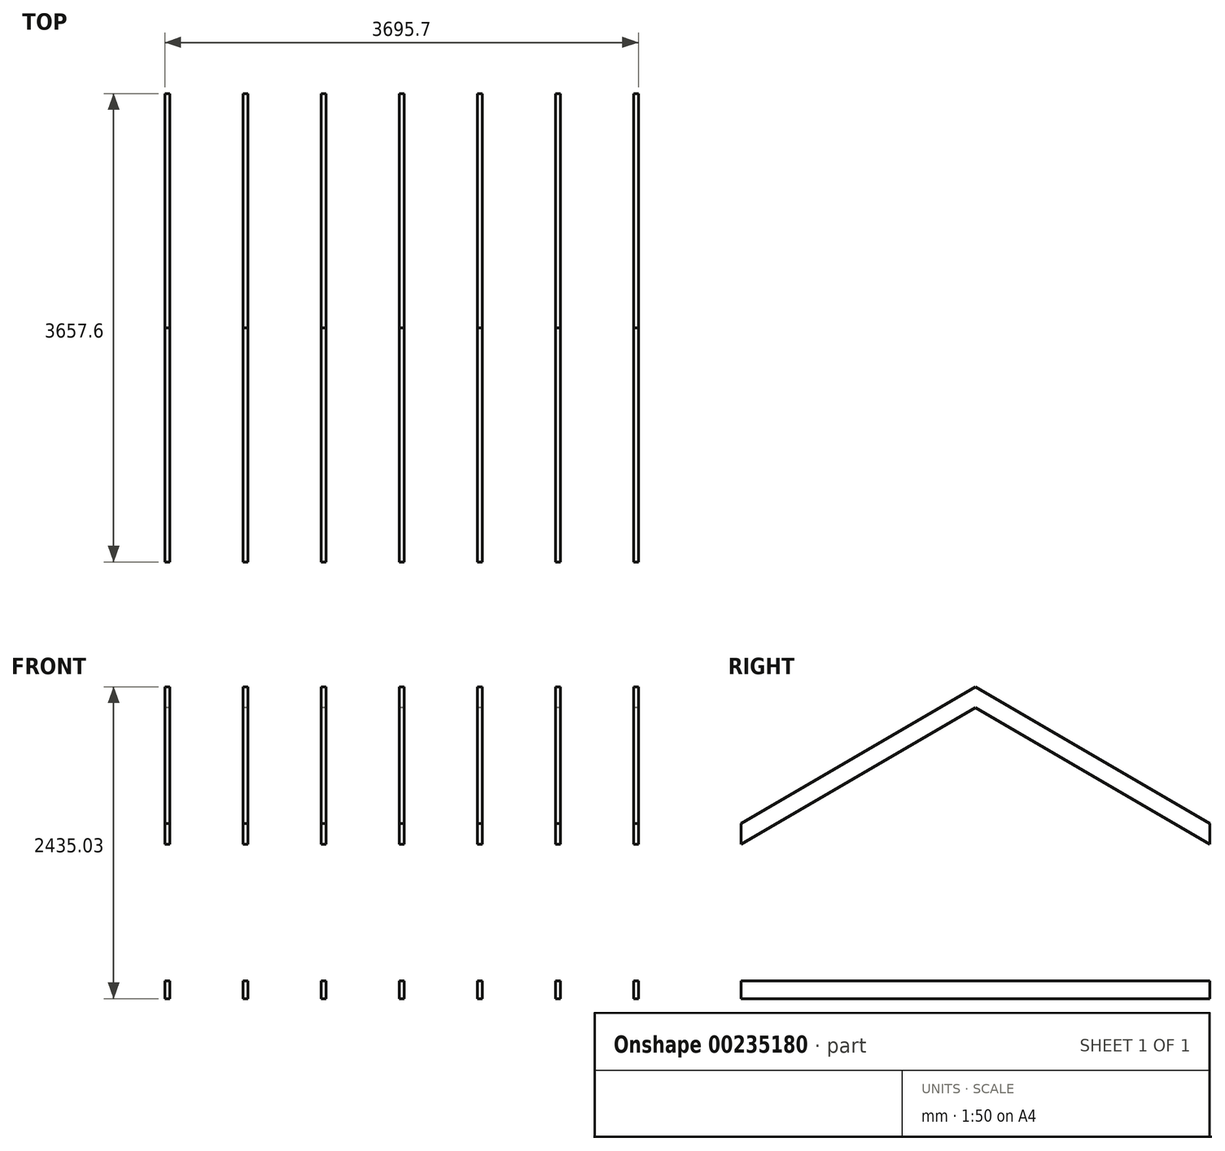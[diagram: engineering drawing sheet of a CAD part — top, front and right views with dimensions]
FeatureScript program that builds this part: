
annotation { "Feature Type Name" : "Feature", "Feature Type Description" : "" }
export const myFeature = defineFeature(function(context is Context, id is Id, definition is map)
    precondition{}
    {
        {
            var Q0;
            Q0=qCreatedBy(makeId("Right.planeOp"),FACE);
            var sketch = newSketch(context, id + "F0", { "sketchPlane" : qUnion([Q0])});
            skLineSegment(sketch, "E0", {"start": v(0, 0) * mm, "end": v(3657.6, 0) * mm});
            skLineSegment(sketch, "E1", {"start": v(3657.6, 0) * mm, "end": v(3657.6, -139.7) * mm});
            skLineSegment(sketch, "E2", {"start": v(3657.6, -139.7) * mm, "end": v(0, -139.7) * mm});
            skLineSegment(sketch, "E3", {"start": v(0, -139.7) * mm, "end": v(0, 0) * mm});
            skLineSegment(sketch, "E4", {"start": v(0, 1066.8) * mm, "end": v(1828.8, 2133.6) * mm});
            skPoint(sketch, "E4.endSnap0", {"position": v(1828.8, 0) * mm});
            skLineSegment(sketch, "E5", {"start": v(1828.8, 2133.6) * mm, "end": v(3657.6, 1066.8) * mm});
            skLineSegment(sketch, "E6", {"start": v(3657.6, 1066.8) * mm, "end": v(3657.6, 1228.53) * mm});
            skLineSegment(sketch, "E7", {"start": v(3657.6, 1228.53) * mm, "end": v(1828.8, 2295.33) * mm});
            skLineSegment(sketch, "E8", {"start": v(1828.8, 2295.33) * mm, "end": v(0, 1228.53) * mm});
            skLineSegment(sketch, "E9", {"start": v(0, 1228.53) * mm, "end": v(0, 1066.8) * mm});
            skSolve(sketch);
        }
        {
            var Q0;
            Q0=makeQuery(id+"F0.imprint","IMPRINT",FACE,{"disambiguationData":[TD([[makeQuery(id+"F0.imprint","IMPRINT",EDGE,{"derivedFrom":sQuery(id+"F0.wireOp",EDGE,"E0")}),-1.0]])]});
            var Q1;
            Q1=makeQuery(id+"F0.imprint","IMPRINT",FACE,{"disambiguationData":[TD([[makeQuery(id+"F0.imprint","IMPRINT",EDGE,{"derivedFrom":sQuery(id+"F0.wireOp",EDGE,"E4")}),1.0]])]});
            extrude(context, id + "F1", {"entities" : qUnion([Q0, Q1]), "depth" : 3962.4 * mm});
        }
        {
            var Q0;
            Q0=makeQuery(id+"F1.opExtrude","SWEPT_FACE",FACE,{"disambiguationData":[OSD([sQuery(id+"F0.wireOp",EDGE,"E9")])]});
            var sketch = newSketch(context, id + "F2", { "sketchPlane" : qUnion([Q0])});
            skLineSegment(sketch, "E10.bottom", {"start": v(3924.3, -139.7) * mm, "end": v(3352.8, -139.7) * mm});
            skLineSegment(sketch, "E10.top", {"start": v(3924.3, 2295.33) * mm, "end": v(3352.8, 2295.33) * mm});
            skLineSegment(sketch, "E10.left", {"start": v(3924.3, -139.7) * mm, "end": v(3924.3, 2295.33) * mm});
            skLineSegment(sketch, "E10.right", {"start": v(3352.8, -139.7) * mm, "end": v(3352.8, 2295.33) * mm});
            skLineSegment(sketch, "E11.1.0.0", {"start": v(3314.7, 2295.33) * mm, "end": v(2743.2, 2295.33) * mm});
            skLineSegment(sketch, "E11.1.0.1", {"start": v(2743.2, -139.7) * mm, "end": v(2743.2, 2295.33) * mm});
            skLineSegment(sketch, "E11.1.0.2", {"start": v(3314.7, -139.7) * mm, "end": v(3314.7, 2295.33) * mm});
            skLineSegment(sketch, "E11.1.0.3", {"start": v(3314.7, -139.7) * mm, "end": v(2743.2, -139.7) * mm});
            skLineSegment(sketch, "E11.2.0.0", {"start": v(2705.1, 2295.33) * mm, "end": v(2133.6, 2295.33) * mm});
            skLineSegment(sketch, "E11.2.0.1", {"start": v(2133.6, -139.7) * mm, "end": v(2133.6, 2295.33) * mm});
            skLineSegment(sketch, "E11.2.0.2", {"start": v(2705.1, -139.7) * mm, "end": v(2705.1, 2295.33) * mm});
            skLineSegment(sketch, "E11.2.0.3", {"start": v(2705.1, -139.7) * mm, "end": v(2133.6, -139.7) * mm});
            skLineSegment(sketch, "E11.3.0.0", {"start": v(2095.5, 2295.33) * mm, "end": v(1524, 2295.33) * mm});
            skLineSegment(sketch, "E11.3.0.1", {"start": v(1524, -139.7) * mm, "end": v(1524, 2295.33) * mm});
            skLineSegment(sketch, "E11.3.0.2", {"start": v(2095.5, -139.7) * mm, "end": v(2095.5, 2295.33) * mm});
            skLineSegment(sketch, "E11.3.0.3", {"start": v(2095.5, -139.7) * mm, "end": v(1524, -139.7) * mm});
            skLineSegment(sketch, "E11.4.0.0", {"start": v(1485.9, 2295.33) * mm, "end": v(914.4, 2295.33) * mm});
            skLineSegment(sketch, "E11.4.0.1", {"start": v(914.4, -139.7) * mm, "end": v(914.4, 2295.33) * mm});
            skLineSegment(sketch, "E11.4.0.2", {"start": v(1485.9, -139.7) * mm, "end": v(1485.9, 2295.33) * mm});
            skLineSegment(sketch, "E11.4.0.3", {"start": v(1485.9, -139.7) * mm, "end": v(914.4, -139.7) * mm});
            skLineSegment(sketch, "E11.5.0.0", {"start": v(876.3, 2295.33) * mm, "end": v(304.8, 2295.33) * mm});
            skLineSegment(sketch, "E11.5.0.1", {"start": v(304.8, -139.7) * mm, "end": v(304.8, 2295.33) * mm});
            skLineSegment(sketch, "E11.5.0.2", {"start": v(876.3, -139.7) * mm, "end": v(876.3, 2295.33) * mm});
            skLineSegment(sketch, "E11.5.0.3", {"start": v(876.3, -139.7) * mm, "end": v(304.8, -139.7) * mm});
            skLineSegment(sketch, "E11.direction1", {"start": v(3352.8, 2295.33) * mm, "end": v(2743.2, 2295.33) * mm, "construction": true});
            skLineSegment(sketch, "E12.bottom", {"start": v(266.7, 2295.33) * mm, "end": v(0, 2295.33) * mm});
            skLineSegment(sketch, "E12.top", {"start": v(266.7, -139.7) * mm, "end": v(0, -139.7) * mm});
            skLineSegment(sketch, "E12.left", {"start": v(266.7, 2295.33) * mm, "end": v(266.7, -139.7) * mm});
            skLineSegment(sketch, "E12.right", {"start": v(0, 2295.33) * mm, "end": v(0, -139.7) * mm});
            skSolve(sketch);
        }
        {
            var Q0;
            {var subQ0=sQuery(id+"F2.wireOp",EDGE,"E12.top");Q0=makeQuery(id+"F2.imprint","IMPRINT",FACE,{"disambiguationData":[TD([[makeQuery(id+"F2.imprint","IMPRINT",EDGE,{"derivedFrom":subQ0}),-1.0]])]});}
            var Q1;
            {var subQ0=sQuery(id+"F2.wireOp",EDGE,"E11.4.0.3");Q1=makeQuery(id+"F2.imprint","IMPRINT",FACE,{"disambiguationData":[TD([[makeQuery(id+"F2.imprint","IMPRINT",EDGE,{"derivedFrom":subQ0}),-1.0]])]});}
            var Q2;
            {var subQ0=sQuery(id+"F2.wireOp",EDGE,"E11.3.0.3");Q2=makeQuery(id+"F2.imprint","IMPRINT",FACE,{"disambiguationData":[TD([[makeQuery(id+"F2.imprint","IMPRINT",EDGE,{"derivedFrom":subQ0}),-1.0]])]});}
            var Q3;
            {var subQ0=sQuery(id+"F2.wireOp",EDGE,"E11.2.0.3");Q3=makeQuery(id+"F2.imprint","IMPRINT",FACE,{"disambiguationData":[TD([[makeQuery(id+"F2.imprint","IMPRINT",EDGE,{"derivedFrom":subQ0}),-1.0]])]});}
            var Q4;
            {var subQ0=sQuery(id+"F2.wireOp",EDGE,"E11.1.0.3");Q4=makeQuery(id+"F2.imprint","IMPRINT",FACE,{"disambiguationData":[TD([[makeQuery(id+"F2.imprint","IMPRINT",EDGE,{"derivedFrom":subQ0}),-1.0]])]});}
            var Q5;
            {var subQ0=sQuery(id+"F2.wireOp",EDGE,"E10.bottom");Q5=makeQuery(id+"F2.imprint","IMPRINT",FACE,{"disambiguationData":[TD([[makeQuery(id+"F2.imprint","IMPRINT",EDGE,{"derivedFrom":subQ0}),-1.0]])]});}
            var Q6;
            {var subQ0=sQuery(id+"F2.wireOp",EDGE,"E10.left");var subQ1=sQuery(id+"F0.wireOp",EDGE,"E9");var subQ2=makeQuery(id+"F1.opExtrude","SWEPT_EDGE",EDGE,{"disambiguationData":[OSD([sQuery(id+"F0.wireOp",EDGE,"E4"),subQ1])]});var subQ3=makeQuery(id+"F2.imprint","INTERSECT",VERTEX,{"derivedFrom":[subQ2,subQ0]});Q6=makeQuery(id+"F2.imprint","IMPRINT",FACE,{"disambiguationData":[TD([[makeQuery(id+"F2.imprint","IMPRINT",EDGE,{"disambiguationData":[TD([[subQ3,-1.0]])],"derivedFrom":subQ0}),1.0]])]});}
            var Q7;
            {var subQ0=sQuery(id+"F2.wireOp",EDGE,"E11.1.0.1");var subQ1=sQuery(id+"F0.wireOp",EDGE,"E9");var subQ2=makeQuery(id+"F1.opExtrude","SWEPT_EDGE",EDGE,{"disambiguationData":[OSD([sQuery(id+"F0.wireOp",EDGE,"E4"),subQ1])]});var subQ3=makeQuery(id+"F2.imprint","INTERSECT",VERTEX,{"derivedFrom":[subQ2,subQ0]});Q7=makeQuery(id+"F2.imprint","IMPRINT",FACE,{"disambiguationData":[TD([[makeQuery(id+"F2.imprint","IMPRINT",EDGE,{"disambiguationData":[TD([[subQ3,-1.0]])],"derivedFrom":subQ0}),-1.0]])]});}
            var Q8;
            {var subQ0=sQuery(id+"F2.wireOp",EDGE,"E11.2.0.1");var subQ1=sQuery(id+"F0.wireOp",EDGE,"E9");var subQ2=makeQuery(id+"F1.opExtrude","SWEPT_EDGE",EDGE,{"disambiguationData":[OSD([sQuery(id+"F0.wireOp",EDGE,"E4"),subQ1])]});var subQ3=makeQuery(id+"F2.imprint","INTERSECT",VERTEX,{"derivedFrom":[subQ2,subQ0]});Q8=makeQuery(id+"F2.imprint","IMPRINT",FACE,{"disambiguationData":[TD([[makeQuery(id+"F2.imprint","IMPRINT",EDGE,{"disambiguationData":[TD([[subQ3,-1.0]])],"derivedFrom":subQ0}),-1.0]])]});}
            var Q9;
            {var subQ0=sQuery(id+"F2.wireOp",EDGE,"E11.3.0.1");var subQ1=sQuery(id+"F0.wireOp",EDGE,"E9");var subQ2=makeQuery(id+"F1.opExtrude","SWEPT_EDGE",EDGE,{"disambiguationData":[OSD([sQuery(id+"F0.wireOp",EDGE,"E4"),subQ1])]});var subQ3=makeQuery(id+"F2.imprint","INTERSECT",VERTEX,{"derivedFrom":[subQ2,subQ0]});Q9=makeQuery(id+"F2.imprint","IMPRINT",FACE,{"disambiguationData":[TD([[makeQuery(id+"F2.imprint","IMPRINT",EDGE,{"disambiguationData":[TD([[subQ3,-1.0]])],"derivedFrom":subQ0}),-1.0]])]});}
            var Q10;
            {var subQ0=sQuery(id+"F2.wireOp",EDGE,"E12.left");var subQ1=sQuery(id+"F0.wireOp",EDGE,"E9");var subQ2=makeQuery(id+"F1.opExtrude","SWEPT_EDGE",EDGE,{"disambiguationData":[OSD([sQuery(id+"F0.wireOp",EDGE,"E8"),subQ1])]});var subQ3=makeQuery(id+"F2.imprint","INTERSECT",VERTEX,{"derivedFrom":[subQ2,subQ0]});Q10=makeQuery(id+"F2.imprint","IMPRINT",FACE,{"disambiguationData":[TD([[makeQuery(id+"F2.imprint","IMPRINT",EDGE,{"disambiguationData":[TD([[subQ3,-1.0]])],"derivedFrom":subQ0}),-1.0]])]});}
            var Q11;
            {var subQ0=sQuery(id+"F2.wireOp",EDGE,"E11.5.0.1");var subQ1=sQuery(id+"F0.wireOp",EDGE,"E9");var subQ2=makeQuery(id+"F1.opExtrude","SWEPT_EDGE",EDGE,{"disambiguationData":[OSD([sQuery(id+"F0.wireOp",EDGE,"E4"),subQ1])]});var subQ3=makeQuery(id+"F2.imprint","INTERSECT",VERTEX,{"derivedFrom":[subQ2,subQ0]});Q11=makeQuery(id+"F2.imprint","IMPRINT",FACE,{"disambiguationData":[TD([[makeQuery(id+"F2.imprint","IMPRINT",EDGE,{"disambiguationData":[TD([[subQ3,-1.0]])],"derivedFrom":subQ0}),-1.0]])]});}
            var Q12;
            {var subQ0=sQuery(id+"F2.wireOp",EDGE,"E11.4.0.1");var subQ1=sQuery(id+"F0.wireOp",EDGE,"E9");var subQ2=makeQuery(id+"F1.opExtrude","SWEPT_EDGE",EDGE,{"disambiguationData":[OSD([sQuery(id+"F0.wireOp",EDGE,"E4"),subQ1])]});var subQ3=makeQuery(id+"F2.imprint","INTERSECT",VERTEX,{"derivedFrom":[subQ2,subQ0]});Q12=makeQuery(id+"F2.imprint","IMPRINT",FACE,{"disambiguationData":[TD([[makeQuery(id+"F2.imprint","IMPRINT",EDGE,{"disambiguationData":[TD([[subQ3,-1.0]])],"derivedFrom":subQ0}),-1.0]])]});}
            var Q13;
            {var subQ0=sQuery(id+"F2.wireOp",EDGE,"E12.bottom");Q13=makeQuery(id+"F2.imprint","IMPRINT",FACE,{"disambiguationData":[TD([[makeQuery(id+"F2.imprint","IMPRINT",EDGE,{"derivedFrom":subQ0}),1.0]])]});}
            var Q14;
            {var subQ0=sQuery(id+"F2.wireOp",EDGE,"E11.5.0.0");Q14=makeQuery(id+"F2.imprint","IMPRINT",FACE,{"disambiguationData":[TD([[makeQuery(id+"F2.imprint","IMPRINT",EDGE,{"derivedFrom":subQ0}),1.0]])]});}
            var Q15;
            {var subQ0=sQuery(id+"F2.wireOp",EDGE,"E11.4.0.0");Q15=makeQuery(id+"F2.imprint","IMPRINT",FACE,{"disambiguationData":[TD([[makeQuery(id+"F2.imprint","IMPRINT",EDGE,{"derivedFrom":subQ0}),1.0]])]});}
            var Q16;
            {var subQ0=sQuery(id+"F2.wireOp",EDGE,"E11.3.0.0");Q16=makeQuery(id+"F2.imprint","IMPRINT",FACE,{"disambiguationData":[TD([[makeQuery(id+"F2.imprint","IMPRINT",EDGE,{"derivedFrom":subQ0}),1.0]])]});}
            var Q17;
            {var subQ0=sQuery(id+"F2.wireOp",EDGE,"E11.2.0.0");Q17=makeQuery(id+"F2.imprint","IMPRINT",FACE,{"disambiguationData":[TD([[makeQuery(id+"F2.imprint","IMPRINT",EDGE,{"derivedFrom":subQ0}),1.0]])]});}
            var Q18;
            {var subQ0=sQuery(id+"F2.wireOp",EDGE,"E11.1.0.0");Q18=makeQuery(id+"F2.imprint","IMPRINT",FACE,{"disambiguationData":[TD([[makeQuery(id+"F2.imprint","IMPRINT",EDGE,{"derivedFrom":subQ0}),1.0]])]});}
            var Q19;
            {var subQ0=sQuery(id+"F2.wireOp",EDGE,"E10.top");Q19=makeQuery(id+"F2.imprint","IMPRINT",FACE,{"disambiguationData":[TD([[makeQuery(id+"F2.imprint","IMPRINT",EDGE,{"derivedFrom":subQ0}),1.0]])]});}
            var Q20;
            {var subQ0=sQuery(id+"F2.wireOp",EDGE,"E11.5.0.3");Q20=makeQuery(id+"F2.imprint","IMPRINT",FACE,{"disambiguationData":[TD([[makeQuery(id+"F2.imprint","IMPRINT",EDGE,{"derivedFrom":subQ0}),-1.0]])]});}
            extrude(context, id + "F3", {"entities" : qUnion([Q0, Q1, Q2, Q3, Q4, Q5, Q6, Q7, Q8, Q9, Q10, Q11, Q12, Q13, Q14, Q15, Q16, Q17, Q18, Q19, Q20]), "operationType" : NewBodyOperationType.REMOVE, "endBound" : BoundingType.THROUGH_ALL, "oppositeDirection" : true, "depth" : 25.4 * mm});
        }
    });
